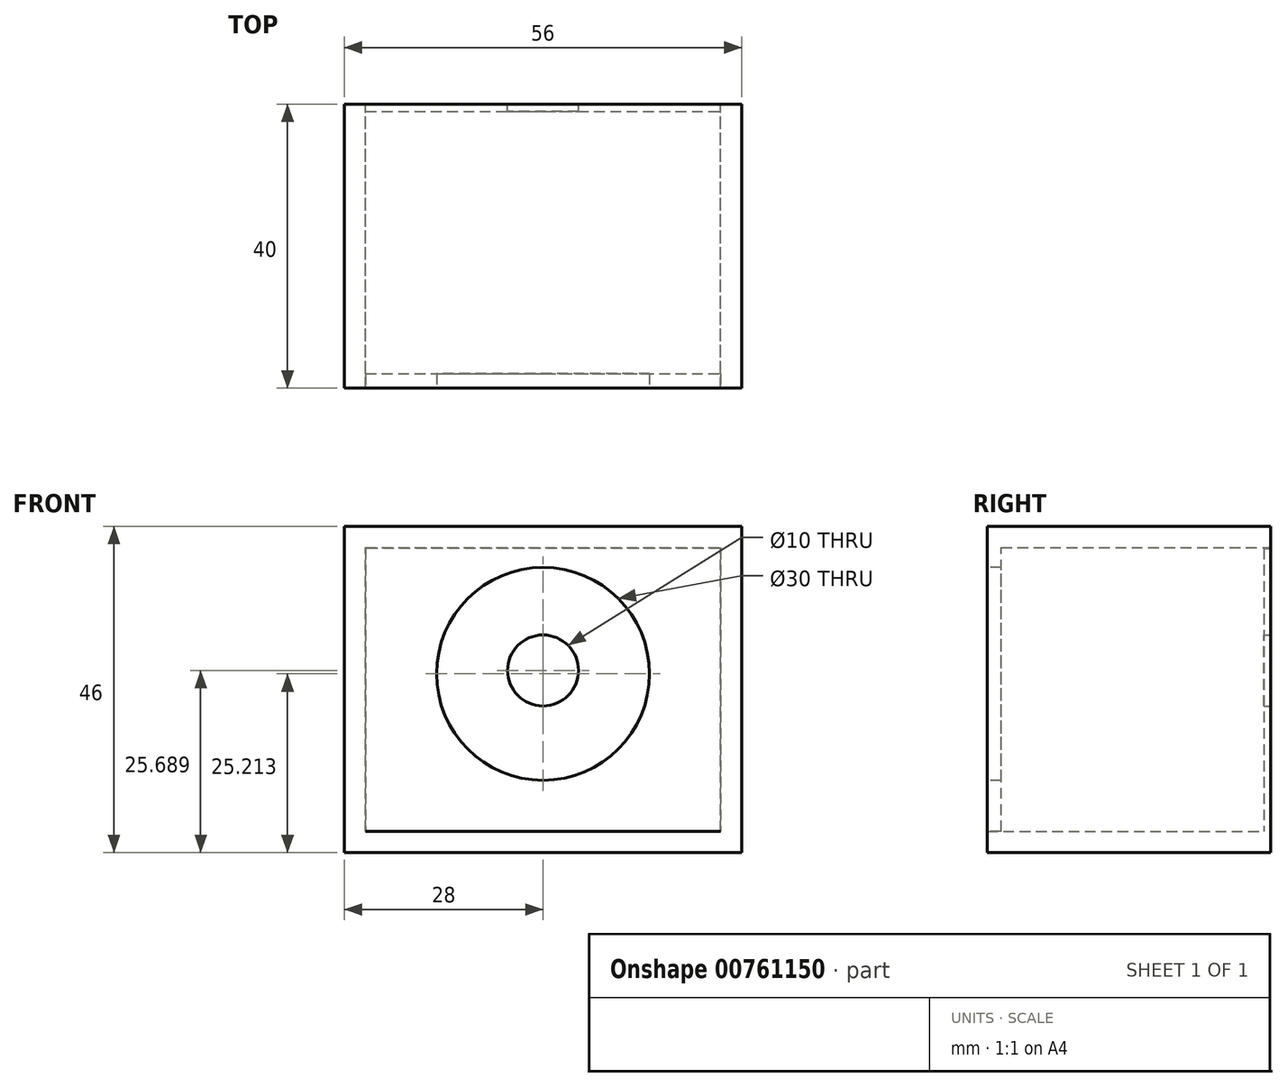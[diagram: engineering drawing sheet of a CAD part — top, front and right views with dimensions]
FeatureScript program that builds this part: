
annotation { "Feature Type Name" : "Feature", "Feature Type Description" : "" }
export const myFeature = defineFeature(function(context is Context, id is Id, definition is map)
    precondition{}
    {
        {
            var Q0;
            Q0=qCreatedBy(makeId("Front.planeOp"),FACE);
            var sketch = newSketch(context, id + "F0", { "sketchPlane" : qUnion([Q0])});
            skLineSegment(sketch, "E0.bottom", {"start": v(-25, 36.53) * mm, "end": v(25, 36.53) * mm});
            skLineSegment(sketch, "E0.top", {"start": v(-25, -3.47) * mm, "end": v(25, -3.47) * mm});
            skLineSegment(sketch, "E0.left", {"start": v(-25, 36.53) * mm, "end": v(-25, -3.47) * mm});
            skLineSegment(sketch, "E0.right", {"start": v(25, 36.53) * mm, "end": v(25, -3.47) * mm});
            skLineSegment(sketch, "E1.bottom", {"start": v(-28, -6.47) * mm, "end": v(28, -6.47) * mm});
            skLineSegment(sketch, "E1.top", {"start": v(-28, 39.53) * mm, "end": v(28, 39.53) * mm});
            skLineSegment(sketch, "E1.left", {"start": v(-28, -6.47) * mm, "end": v(-28, 39.53) * mm});
            skLineSegment(sketch, "E1.right", {"start": v(28, -6.47) * mm, "end": v(28, 39.53) * mm});
            skLineSegment(sketch, "E2", {"start": v(0, 28.26) * mm, "end": v(0, -21.24) * mm});
            skLineSegment(sketch, "E3", {"start": v(35.82, 26.53) * mm, "end": v(-17.7, 26.53) * mm});
            skSolve(sketch);
        }
        {
            var Q0;
            Q0 = qSketchRegion(id + "F0", true);
            extrude(context, id + "F1", {"entities" : qUnion([Q0]), "endBound" : BoundingType.SYMMETRIC, "depth" : 40 * mm, "offsetDistance" : 25 * mm});
        }
        {
            var Q0;
            Q0=qCreatedBy(makeId("Front.planeOp"),FACE);
            cPlane(context, id + "F2", {"entities" : qUnion([Q0]), "cplaneType" : CPlaneType.OFFSET, "offset" : 20 * mm, "width" : 150 * mm, "height" : 150 * mm});
        }
        {
            var Q0;
            Q0=qCreatedBy(makeId("Front.planeOp"),FACE);
            cPlane(context, id + "F3", {"entities" : qUnion([Q0]), "cplaneType" : CPlaneType.OFFSET, "offset" : 20 * mm, "oppositeDirection" : true, "width" : 150 * mm, "height" : 150 * mm});
        }
        {
            var Q0;
            Q0=qCreatedBy(id+"F3.planeOp",FACE);
            var sketch = newSketch(context, id + "F4", { "sketchPlane" : qUnion([Q0])});
            skLineSegment(sketch, "E4.bottom", {"start": v(25, 36.4) * mm, "end": v(-25, 36.4) * mm});
            skLineSegment(sketch, "E4.top", {"start": v(25, -3.6) * mm, "end": v(-25, -3.6) * mm});
            skLineSegment(sketch, "E4.left", {"start": v(25, 36.4) * mm, "end": v(25, -3.6) * mm});
            skLineSegment(sketch, "E4.right", {"start": v(-25, 36.4) * mm, "end": v(-25, -3.6) * mm});
            skLineSegment(sketch, "E5", {"start": v(0, 26.92) * mm, "end": v(0, -17.28) * mm});
            skCircle(sketch, "E6", {"center": v(0, 19.22) * mm, "radius": 5 * mm});
            skSolve(sketch);
        }
        {
            var Q0;
            Q0 = qSketchRegion(id + "F4", true);
            var Q1;
            Q1 = qSketchRegion(id + "F6", true);
            extrude(context, id + "F5", {"entities" : qUnion([Q0, Q1]), "operationType" : NewBodyOperationType.ADD, "depth" : 1 * mm, "offsetDistance" : 25 * mm});
        }
        {
            var Q0;
            Q0=qCreatedBy(id+"F2.planeOp",FACE);
            var sketch = newSketch(context, id + "F6", { "sketchPlane" : qUnion([Q0])});
            skLineSegment(sketch, "E7.bottom", {"start": v(-25, -3.45) * mm, "end": v(25, -3.45) * mm});
            skLineSegment(sketch, "E7.top", {"start": v(-25, 36.55) * mm, "end": v(25, 36.55) * mm});
            skLineSegment(sketch, "E7.left", {"start": v(-25, -3.45) * mm, "end": v(-25, 36.55) * mm});
            skLineSegment(sketch, "E7.right", {"start": v(25, -3.45) * mm, "end": v(25, 36.55) * mm});
            skLineSegment(sketch, "E8", {"start": v(0, 18.74) * mm, "end": v(0, -10.85) * mm});
            skCircle(sketch, "E9", {"center": v(0, 18.74) * mm, "radius": 15 * mm});
            skSolve(sketch);
        }
        {
            var Q0;
            Q0=makeQuery(id+"F6.imprint","IMPRINT",FACE,{"disambiguationData":[TD([[makeQuery(id+"F6.imprint","IMPRINT",EDGE,{"derivedFrom":sQuery(id+"F6.wireOp",EDGE,"E7.top")}),-1.0]])]});
            extrude(context, id + "F7", {"entities" : qUnion([Q0]), "operationType" : NewBodyOperationType.ADD, "oppositeDirection" : true, "depth" : 2 * mm, "offsetDistance" : 25 * mm});
        }
    });
